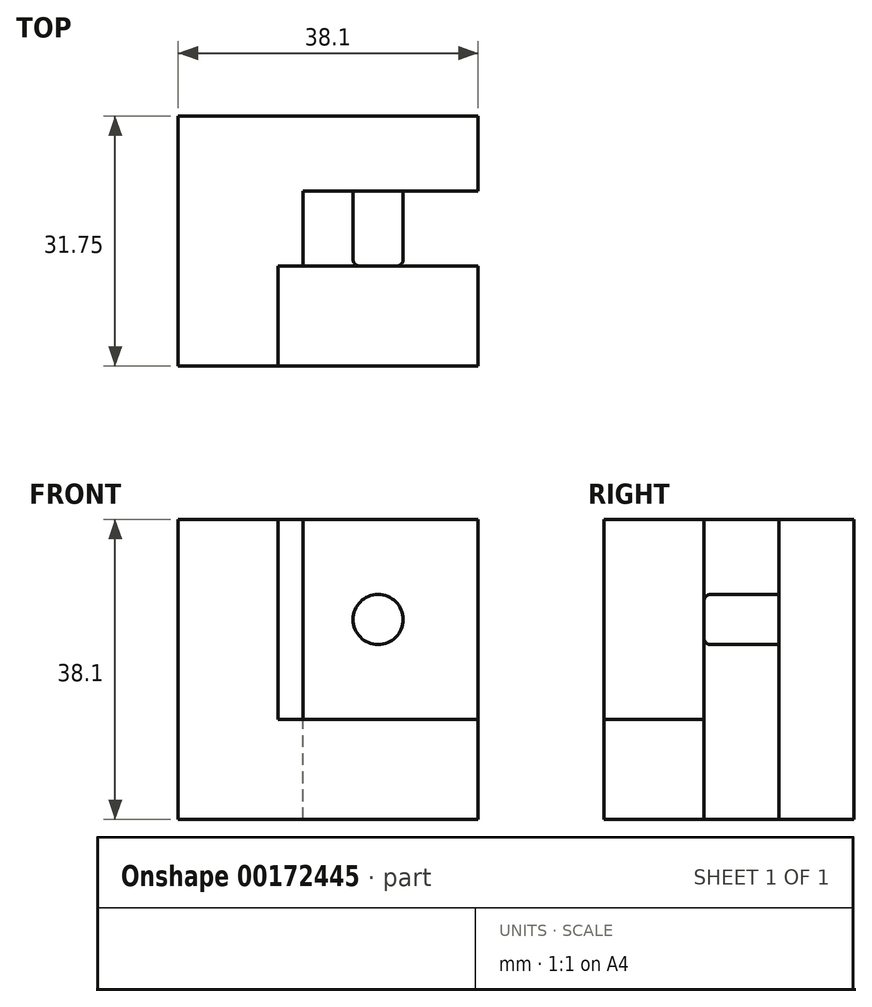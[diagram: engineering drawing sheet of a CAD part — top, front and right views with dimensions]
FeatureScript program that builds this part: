
annotation { "Feature Type Name" : "Feature", "Feature Type Description" : "" }
export const myFeature = defineFeature(function(context is Context, id is Id, definition is map)
    precondition{}
    {
        {
            var Q0;
            Q0=qCreatedBy(makeId("Top.planeOp"),FACE);
            var sketch = newSketch(context, id + "F0", { "sketchPlane" : qUnion([Q0])});
            skLineSegment(sketch, "E0.bottom", {"start": v(0, 0) * mm, "end": v(38.1, 0) * mm});
            skLineSegment(sketch, "E0.top", {"start": v(0, -31.75) * mm, "end": v(38.1, -31.75) * mm});
            skLineSegment(sketch, "E0.left", {"start": v(0, 0) * mm, "end": v(0, -31.75) * mm});
            skLineSegment(sketch, "E0.right", {"start": v(38.1, 0) * mm, "end": v(38.1, -31.75) * mm});
            skSolve(sketch);
        }
        {
            var Q0;
            Q0=makeQuery(id+"F0.imprint","IMPRINT",FACE,{"disambiguationData":[TD([[makeQuery(id+"F0.imprint","IMPRINT",EDGE,{"derivedFrom":sQuery(id+"F0.wireOp",EDGE,"E0.bottom")}),-1.0]])]});
            extrude(context, id + "F1", {"entities" : qUnion([Q0]), "depth" : 38.1 * mm});
        }
        {
            var Q0;
            Q0=makeQuery(id+"F1.opExtrude","SWEPT_FACE",FACE,{"disambiguationData":[OSD([sQuery(id+"F0.wireOp",EDGE,"E0.top")])]});
            var sketch = newSketch(context, id + "F2", { "sketchPlane" : qUnion([Q0])});
            skLineSegment(sketch, "E1.bottom", {"start": v(38.1, 38.1) * mm, "end": v(12.7, 38.1) * mm});
            skLineSegment(sketch, "E1.top", {"start": v(38.1, 12.7) * mm, "end": v(12.7, 12.7) * mm});
            skLineSegment(sketch, "E1.left", {"start": v(38.1, 38.1) * mm, "end": v(38.1, 12.7) * mm});
            skLineSegment(sketch, "E1.right", {"start": v(12.7, 38.1) * mm, "end": v(12.7, 12.7) * mm});
            skSolve(sketch);
        }
        {
            var Q0;
            Q0=makeQuery(id+"F2.imprint","IMPRINT",FACE,{"disambiguationData":[TD([[makeQuery(id+"F2.imprint","IMPRINT",EDGE,{"derivedFrom":sQuery(id+"F2.wireOp",EDGE,"E1.bottom")}),-1.0]])]});
            extrude(context, id + "F3", {"entities" : qUnion([Q0]), "operationType" : NewBodyOperationType.REMOVE, "oppositeDirection" : true, "depth" : 12.7 * mm});
        }
        {
            var Q0;
            Q0=makeQuery(id+"F1.opExtrude","CAP_FACE",FACE,{"disambiguationData":[OSD([sQuery(id+"F0.wireOp",EDGE,"E0.bottom"),sQuery(id+"F0.wireOp",EDGE,"E0.top"),sQuery(id+"F0.wireOp",EDGE,"E0.left"),sQuery(id+"F0.wireOp",EDGE,"E0.right")])],"isStart":false});
            var sketch = newSketch(context, id + "F4", { "sketchPlane" : qUnion([Q0])});
            skLineSegment(sketch, "E2.bottom", {"start": v(38.1, -19.05) * mm, "end": v(15.88, -19.05) * mm});
            skLineSegment(sketch, "E2.top", {"start": v(38.1, -9.53) * mm, "end": v(15.88, -9.53) * mm});
            skLineSegment(sketch, "E2.left", {"start": v(38.1, -19.05) * mm, "end": v(38.1, -9.53) * mm});
            skLineSegment(sketch, "E2.right", {"start": v(15.88, -19.05) * mm, "end": v(15.88, -9.53) * mm});
            skSolve(sketch);
        }
        {
            var Q0;
            Q0=makeQuery(id+"F4.imprint","IMPRINT",FACE,{"disambiguationData":[TD([[makeQuery(id+"F4.imprint","IMPRINT",EDGE,{"derivedFrom":sQuery(id+"F4.wireOp",EDGE,"E2.bottom")}),1.0]])]});
            extrude(context, id + "F5", {"entities" : qUnion([Q0]), "operationType" : NewBodyOperationType.REMOVE, "endBound" : BoundingType.THROUGH_ALL, "oppositeDirection" : true, "depth" : 25.4 * mm});
        }
        {
            var Q0;
            Q0=makeQuery(id+"F5.boolean.opBoolean","COPY",FACE,{"derivedFrom":makeQuery(id+"F5.opExtrude","SWEPT_FACE",FACE,{"disambiguationData":[OSD([sQuery(id+"F4.wireOp",EDGE,"E2.top")])]})});
            var sketch = newSketch(context, id + "F6", { "sketchPlane" : qUnion([Q0])});
            skCircle(sketch, "E3", {"center": v(25.4, 25.4) * mm, "radius": 3.18 * mm});
            skSolve(sketch);
        }
        {
            var Q0;
            Q0=makeQuery(id+"F6.imprint","IMPRINT",FACE,{"disambiguationData":[TD([[makeQuery(id+"F6.imprint","IMPRINT",EDGE,{"derivedFrom":sQuery(id+"F6.wireOp",EDGE,"E3")}),1.0]])]});
            extrude(context, id + "F7", {"entities" : qUnion([Q0]), "operationType" : NewBodyOperationType.ADD, "depth" : 9.52 * mm});
        }
        {
            var Q0;
            Q0=makeQuery(id+"F7.opExtrude","CAP_EDGE",EDGE,{"disambiguationData":[OSD([sQuery(id+"F6.wireOp",EDGE,"E3")])],"isStart":false});
            fillet(context, id + "F8", {"entities" : qUnion([Q0]), "radius" : 0.8 * mm, "tangentPropagation" : true, "allowEdgeOverflow" : false});
        }
    });
